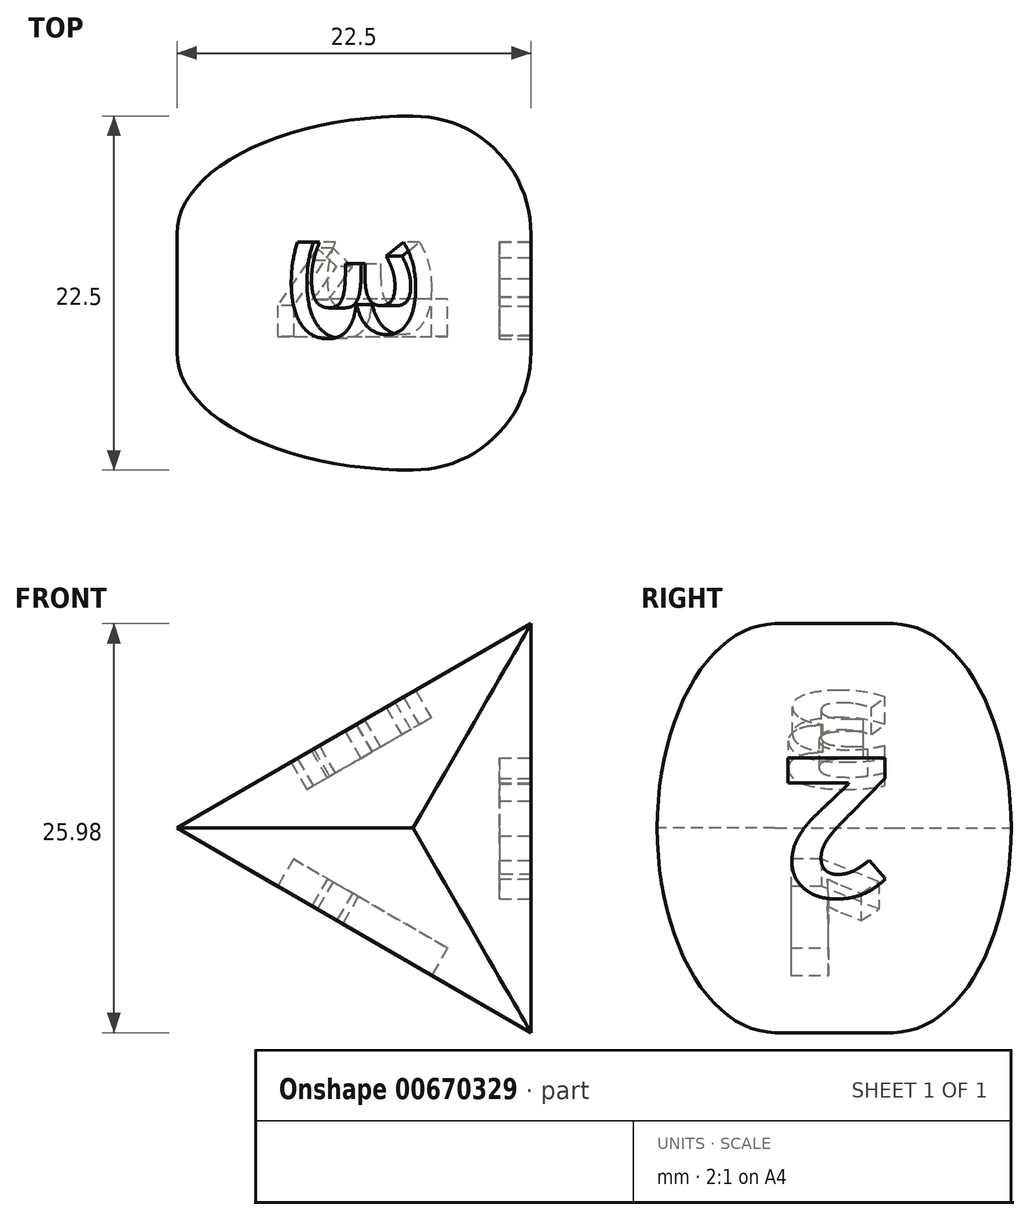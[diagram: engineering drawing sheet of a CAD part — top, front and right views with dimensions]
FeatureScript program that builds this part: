
annotation { "Feature Type Name" : "Feature", "Feature Type Description" : "" }
export const myFeature = defineFeature(function(context is Context, id is Id, definition is map)
    precondition{}
    {
        {
            var Q0;
            Q0=qCreatedBy(makeId("Front.planeOp"),FACE);
            var sketch = newSketch(context, id + "F0", { "sketchPlane" : qUnion([Q0])});
            skCircle(sketch, "E0.cCircle", {"center": v(0, 0) * mm, "radius": 7.5 * mm, "construction": true});
            skLineSegment(sketch, "E0.0", {"start": v(7.5, 13) * mm, "end": v(7.5, -13) * mm});
            skLineSegment(sketch, "E0.1", {"start": v(7.5, -13) * mm, "end": v(-15, 0) * mm});
            skLineSegment(sketch, "E0.2", {"start": v(-15, 0) * mm, "end": v(7.5, 13) * mm});
            skPoint(sketch, "E0.0.midPoint", {"position": v(7.5, 0) * mm});
            skSolve(sketch);
        }
        {
            var Q0;
            Q0=makeQuery(id+"F0.imprint","IMPRINT",FACE,{"disambiguationData":[TD([[makeQuery(id+"F0.imprint","IMPRINT",EDGE,{"derivedFrom":sQuery(id+"F0.wireOp",EDGE,"E0.0")}),-1.0]])]});
            extrude(context, id + "F1", {"entities" : qUnion([Q0]), "depth" : 11.25 * mm, "offsetDistance" : 25 * mm, "hasSecondDirection" : true, "secondDirectionOppositeDirection" : true, "secondDirectionDepth" : 11.25 * mm});
        }
        {
            var Q0;
            Q0=makeQuery(id+"F1.opExtrude","CAP_FACE",FACE,{"disambiguationData":[OSD([sQuery(id+"F0.wireOp",EDGE,"E0.0"),sQuery(id+"F0.wireOp",EDGE,"E0.1"),sQuery(id+"F0.wireOp",EDGE,"E0.2")])],"isStart":true});
            var Q1;
            Q1=makeQuery(id+"F1.opExtrude","CAP_FACE",FACE,{"disambiguationData":[OSD([sQuery(id+"F0.wireOp",EDGE,"E0.0"),sQuery(id+"F0.wireOp",EDGE,"E0.1"),sQuery(id+"F0.wireOp",EDGE,"E0.2")])],"isStart":false});
            fillet(context, id + "F2", {"entities" : qUnion([Q0, Q1]), "radius" : 7.5 * mm, "tangentPropagation" : true, "allowEdgeOverflow" : false});
        }
        {
            var Q0;
            Q0=makeQuery(id+"F1.opExtrude","SWEPT_FACE",FACE,{"disambiguationData":[OSD([sQuery(id+"F0.wireOp",EDGE,"E0.1")])]});
            var sketch = newSketch(context, id + "F3", { "sketchPlane" : qUnion([Q0])});
            skText(sketch, "E1", { "text": "1", "fontName": "OpenSans-Bold.ttf"});
            skLineSegment(sketch, "E2", {"start": v(0, -3.75) * mm, "end": v(0, 3.75) * mm});
            skPoint(sketch, "E3", {"position": v(0, 0) * mm});
            const initialGuessF3  = {"E1": [0.0057, -0.00378, 0, 1, 0.0114]};
            skSetInitialGuess(sketch, initialGuessF3);
            skSolve(sketch);
        }
        {
            var Q0;
            Q0=makeQuery(id+"F1.opExtrude","SWEPT_FACE",FACE,{"disambiguationData":[OSD([sQuery(id+"F0.wireOp",EDGE,"E0.0")])]});
            var sketch = newSketch(context, id + "F4", { "sketchPlane" : qUnion([Q0])});
            skLineSegment(sketch, "E4", {"start": v(3.75, 0) * mm, "end": v(-3.75, 0) * mm});
            skPoint(sketch, "E5", {"position": v(0, 0) * mm});
            skText(sketch, "E6", { "text": "2", "fontName": "OpenSans-Bold.ttf"});
            skLineSegment(sketch, "E7", {"start": v(3.73, 0) * mm, "end": v(-3.73, 0) * mm});
            const initialGuessF4  = {"E6": [0.00373, 0.00445, -1, 0, 0.0089]};
            skSetInitialGuess(sketch, initialGuessF4);
            skSolve(sketch);
        }
        {
            var Q0;
            Q0=makeQuery(id+"F1.opExtrude","SWEPT_FACE",FACE,{"disambiguationData":[OSD([sQuery(id+"F0.wireOp",EDGE,"E0.2")])]});
            var sketch = newSketch(context, id + "F5", { "sketchPlane" : qUnion([Q0])});
            skLineSegment(sketch, "E8", {"start": v(0, 3.75) * mm, "end": v(0, -3.75) * mm});
            skLineSegment(sketch, "E9", {"start": v(0, -3.75) * mm, "end": v(0, 0) * mm});
            skText(sketch, "E10", { "text": "3", "fontName": "OpenSans-Bold.ttf"});
            skLineSegment(sketch, "E11", {"start": v(0, 0) * mm, "end": v(0, -3.75) * mm});
            const initialGuessF5  = {"E10": [-0.00448, 0.00371, 0, -1, 0.00895]};
            skSetInitialGuess(sketch, initialGuessF5);
            skSolve(sketch);
        }
        {
            var Q0;
            {var subQ0=sQuery(id+"F3.wireOp",EDGE,"E1.sketch_text.stroke-0");Q0=makeQuery(id+"F3.imprint","IMPRINT",FACE,{"disambiguationData":[TD([[makeQuery(id+"F3.imprint","IMPRINT",EDGE,{"derivedFrom":subQ0}),-1.0]])]});}
            var Q1;
            {var subQ0=sQuery(id+"F3.wireOp",EDGE,"E1.sketch_text.stroke-2");Q1=makeQuery(id+"F3.imprint","IMPRINT",FACE,{"disambiguationData":[TD([[makeQuery(id+"F3.imprint","IMPRINT",EDGE,{"derivedFrom":subQ0}),-1.0]])]});}
            extrude(context, id + "F6", {"entities" : qUnion([Q0, Q1]), "operationType" : NewBodyOperationType.REMOVE, "oppositeDirection" : true, "depth" : 2 * mm, "offsetDistance" : 25 * mm});
        }
        {
            var Q0;
            {var subQ0=sQuery(id+"F4.wireOp",EDGE,"E6.sketch_text.stroke-4");Q0=makeQuery(id+"F4.imprint","IMPRINT",FACE,{"disambiguationData":[TD([[makeQuery(id+"F4.imprint","IMPRINT",EDGE,{"derivedFrom":subQ0}),-1.0]])]});}
            var Q1;
            Q1=makeQuery(id+"F4.imprint","IMPRINT",FACE,{"disambiguationData":[TD([[makeQuery(id+"F4.imprint","IMPRINT",EDGE,{"derivedFrom":sQuery(id+"F4.wireOp",EDGE,"E6.sketch_text.stroke-0")}),-1.0]])]});
            extrude(context, id + "F7", {"entities" : qUnion([Q0, Q1]), "operationType" : NewBodyOperationType.REMOVE, "oppositeDirection" : true, "depth" : 2 * mm, "offsetDistance" : 25 * mm});
        }
        {
            var Q0;
            Q0 = qSketchRegion(id + "F5", true);
            extrude(context, id + "F8", {"entities" : qUnion([Q0]), "operationType" : NewBodyOperationType.REMOVE, "oppositeDirection" : true, "depth" : 2 * mm, "offsetDistance" : 25 * mm});
        }
    });
